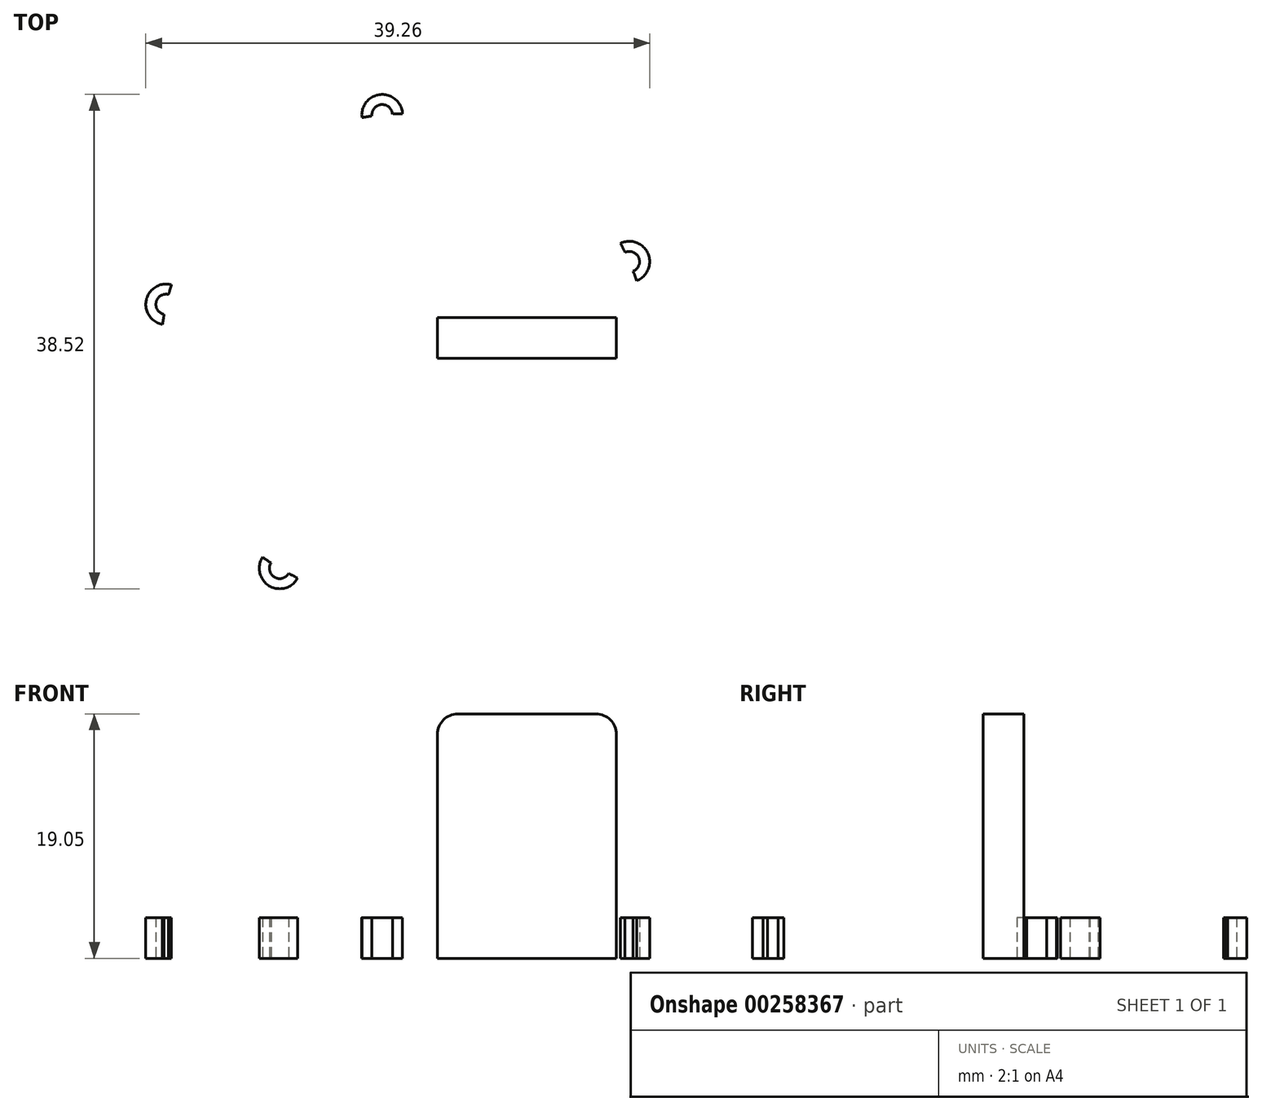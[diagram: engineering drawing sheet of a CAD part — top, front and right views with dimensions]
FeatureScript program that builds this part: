
annotation { "Feature Type Name" : "Feature", "Feature Type Description" : "" }
export const myFeature = defineFeature(function(context is Context, id is Id, definition is map)
    precondition{}
    {
        {
            var Q0;
            Q0=qCreatedBy(makeId("Top.planeOp"),FACE);
            var sketch = newSketch(context, id + "F0", { "sketchPlane" : qUnion([Q0])});
            skLineSegment(sketch, "E0", {"start": v(0, 0) * mm, "end": v(19.05, 0) * mm});
            skLineSegment(sketch, "E1", {"start": v(19.05, 0) * mm, "end": v(0, 0) * mm});
            skLineSegment(sketch, "E2", {"start": v(0, 0) * mm, "end": v(0, -19.05) * mm});
            skArc(sketch, "E3", {"start": v(19.05, 0) * mm, "mid": v(-13.47, 13.47) * mm, "end": v(0, -19.05) * mm});
            skCircle(sketch, "E4", {"center": v(-9.73, -16.38) * mm, "radius": 0.8 * mm});
            skArc(sketch, "E5", {"start": v(-11.06, -15.5) * mm, "mid": v(-10.55, -17.74) * mm, "end": v(-8.34, -17.13) * mm});
            skArc(sketch, "E6.2.0", {"start": v(18.07, 6.04) * mm, "mid": v(18.96, 8.15) * mm, "end": v(16.81, 8.96) * mm});
            skCircle(sketch, "E6.2.1", {"center": v(17.5, 7.53) * mm, "radius": 0.8 * mm});
            skArc(sketch, "E6.3.0", {"start": v(-0.16, 19.05) * mm, "mid": v(-1.9, 20.55) * mm, "end": v(-3.32, 18.76) * mm});
            skCircle(sketch, "E6.3.1", {"center": v(-1.75, 18.97) * mm, "radius": 0.8 * mm});
            skArc(sketch, "E6.4.0", {"start": v(-18.17, 5.73) * mm, "mid": v(-20.13, 4.55) * mm, "end": v(-18.87, 2.64) * mm});
            skCircle(sketch, "E6.4.1", {"center": v(-18.58, 4.2) * mm, "radius": 0.8 * mm});
            skLineSegment(sketch, "E7", {"start": v(16.5, 0) * mm, "end": v(16.5, 3.18) * mm});
            skLineSegment(sketch, "E8.MirrorCS", {"start": v(2.55, 0) * mm, "end": v(2.55, 3.18) * mm});
            skLineSegment(sketch, "E9", {"start": v(16.5, 3.18) * mm, "end": v(2.55, 3.18) * mm});
            skSolve(sketch);
        }
        {
            var Q0;
            {var subQ0=sQuery(id+"F0.wireOp",EDGE,"E5");Q0=makeQuery(id+"F0.imprint","IMPRINT",FACE,{"disambiguationData":[TD([[makeQuery(id+"F0.imprint","IMPRINT",EDGE,{"derivedFrom":subQ0}),1.0]])]});}
            var Q1;
            {var subQ0=sQuery(id+"F0.wireOp",EDGE,"E6.4.0");Q1=makeQuery(id+"F0.imprint","IMPRINT",FACE,{"disambiguationData":[TD([[makeQuery(id+"F0.imprint","IMPRINT",EDGE,{"derivedFrom":subQ0}),1.0]])]});}
            var Q2;
            {var subQ0=sQuery(id+"F0.wireOp",EDGE,"E6.3.0");Q2=makeQuery(id+"F0.imprint","IMPRINT",FACE,{"disambiguationData":[TD([[makeQuery(id+"F0.imprint","IMPRINT",EDGE,{"derivedFrom":subQ0}),1.0]])]});}
            var Q3;
            {var subQ0=sQuery(id+"F0.wireOp",EDGE,"E6.2.0");Q3=makeQuery(id+"F0.imprint","IMPRINT",FACE,{"disambiguationData":[TD([[makeQuery(id+"F0.imprint","IMPRINT",EDGE,{"derivedFrom":subQ0}),1.0]])]});}
            var Q4;
            {var subQ13=sQuery(id+"F0.wireOp",EDGE,"E1");Q4=makeQuery(id+"F0.imprint","IMPRINT",FACE,{"disambiguationData":[TD([[makeQuery(id+"F0.imprint","IMPRINT",EDGE,{"derivedFrom":subQ13}),-1.0]])]});}
            extrude(context, id + "F1", {"entities" : qUnion([Q0, Q1, Q2, Q3, Q4]), "depth" : 3.17 * mm});
        }
        {
            var Q0;
            {var subQ0=sQuery(id+"F0.wireOp",EDGE,"E7");Q0=makeQuery(id+"F0.imprint","IMPRINT",FACE,{"disambiguationData":[TD([[makeQuery(id+"F0.imprint","IMPRINT",EDGE,{"derivedFrom":subQ0}),1.0]])]});}
            extrude(context, id + "F2", {"entities" : qUnion([Q0]), "operationType" : NewBodyOperationType.ADD, "depth" : 19.05 * mm});
        }
        {
            var Q0;
            Q0=makeQuery(id+"F2.opExtrude","SWEPT_FACE",FACE,{"disambiguationData":[OSD([sQuery(id+"F0.wireOp",EDGE,"E9")])]});
            var sketch = newSketch(context, id + "F3", { "sketchPlane" : qUnion([Q0])});
            skLineSegment(sketch, "E10", {"start": v(-9.53, 19.05) * mm, "end": v(-9.53, 17.36) * mm, "construction": true});
            skPoint(sketch, "E10.endSnap0", {"position": v(-9.53, 19.05) * mm});
            skLineSegment(sketch, "E11", {"start": v(-9.53, 17.36) * mm, "end": v(-9.53, 18.2) * mm, "construction": true});
            skLineSegment(sketch, "E12", {"start": v(-9.53, 18.2) * mm, "end": v(-3.9, 18.2) * mm, "construction": true});
            skLineSegment(sketch, "E13.MirrorCS", {"start": v(-9.53, 18.2) * mm, "end": v(-15.15, 18.2) * mm, "construction": true});
            skSolve(sketch);
        }
        {
            var Q0;
            Q0=makeQuery(id+"F2.opExtrude","CAP_EDGE",EDGE,{"disambiguationData":[OSD([sQuery(id+"F0.wireOp",EDGE,"E8.MirrorCS")])],"isStart":false});
            var Q1;
            Q1=makeQuery(id+"F2.opExtrude","CAP_EDGE",EDGE,{"disambiguationData":[OSD([sQuery(id+"F0.wireOp",EDGE,"E7")])],"isStart":false});
            fillet(context, id + "F4", {"entities" : qUnion([Q0, Q1]), "radius" : 1.6 * mm, "tangentPropagation" : true, "allowEdgeOverflow" : false});
        }
        {
            var Q0;
            Q0=sQuery(id+"F3.wireOp",VERTEX,"E12.end");
            var Q1;
            Q1=sQuery(id+"F3.wireOp",VERTEX,"E13.MirrorCS.end");
            var Q2;
            Q2=makeQuery(id+"F1.opExtrude","SWEPT_BODY",BODY,{"disambiguationData":[OSD([sQuery(id+"F0.wireOp",EDGE,"E1"),sQuery(id+"F0.wireOp",EDGE,"E2"),sQuery(id+"F0.wireOp",EDGE,"E3"),sQuery(id+"F0.wireOp",EDGE,"E4"),sQuery(id+"F0.wireOp",EDGE,"E5"),sQuery(id+"F0.wireOp",EDGE,"E6.2.0"),sQuery(id+"F0.wireOp",EDGE,"E6.2.1"),sQuery(id+"F0.wireOp",EDGE,"E6.3.0"),sQuery(id+"F0.wireOp",EDGE,"E6.3.1"),sQuery(id+"F0.wireOp",EDGE,"E6.4.0"),sQuery(id+"F0.wireOp",EDGE,"E6.4.1"),sQuery(id+"F0.wireOp",EDGE,"E7"),sQuery(id+"F0.wireOp",EDGE,"E8.MirrorCS"),sQuery(id+"F0.wireOp",EDGE,"E9")])]});
            hole(context, id + "F5", {"style" : HoleStyle.SIMPLE, "endStyle" : HoleEndStyle.THROUGH, "holeDiameter" : 0.79 * mm, "tappedDepth" : 12.7 * mm, "tapClearance" : 3, "locations" : qUnion([Q0, Q1]), "scope" : qUnion([Q2])});
        }
    });
